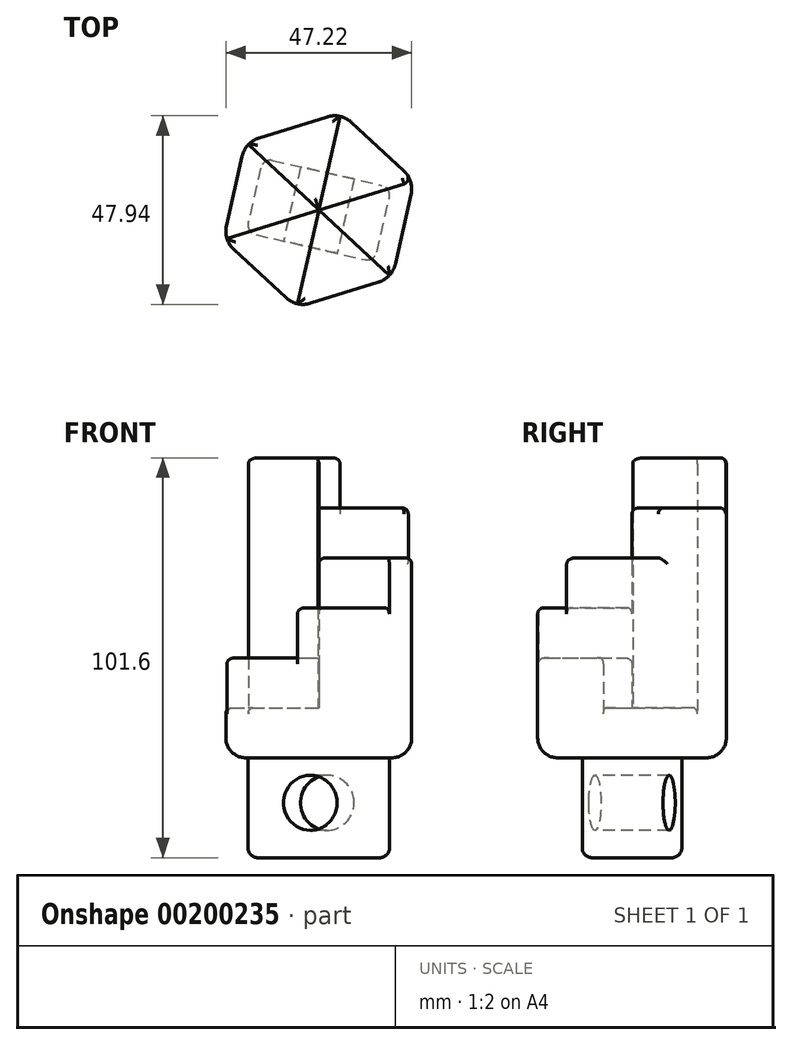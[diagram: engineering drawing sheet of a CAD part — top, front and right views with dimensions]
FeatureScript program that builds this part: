
annotation { "Feature Type Name" : "Feature", "Feature Type Description" : "" }
export const myFeature = defineFeature(function(context is Context, id is Id, definition is map)
    precondition{}
    {
        {
            var Q0;
            Q0=qCreatedBy(makeId("Top.planeOp"),FACE);
            var sketch = newSketch(context, id + "F0", { "sketchPlane" : qUnion([Q0])});
            skLineSegment(sketch, "E0.0", {"start": v(23.45, 3.92) * mm, "end": v(19.44, -13.7) * mm});
            skLineSegment(sketch, "E0.1", {"start": v(15.12, -18.35) * mm, "end": v(-2.14, -23.68) * mm});
            skLineSegment(sketch, "E0.2", {"start": v(-8.33, -22.27) * mm, "end": v(-21.58, -10) * mm});
            skLineSegment(sketch, "E0.3", {"start": v(-23.45, -3.92) * mm, "end": v(-19.44, 13.7) * mm});
            skLineSegment(sketch, "E0.4", {"start": v(-15.12, 18.35) * mm, "end": v(2.14, 23.68) * mm});
            skLineSegment(sketch, "E0.5", {"start": v(8.33, 22.27) * mm, "end": v(21.58, 10) * mm});
            skPoint(sketch, "E1", {"position": v(0, 0) * mm});
            skLineSegment(sketch, "E2", {"start": v(-24.27, -7.5) * mm, "end": v(24.27, 7.5) * mm});
            skLineSegment(sketch, "E3", {"start": v(-18.63, 17.27) * mm, "end": v(18.63, -17.27) * mm});
            skLineSegment(sketch, "E4", {"start": v(5.64, 24.77) * mm, "end": v(-5.64, -24.77) * mm});
            skPoint(sketch, "E5.visualSharp", {"position": v(-18.63, 17.27) * mm});
            skArc(sketch, "E5.filletArc", {"start": v(-15.12, 18.35) * mm, "mid": v(-17.9, 16.6) * mm, "end": v(-19.44, 13.7) * mm});
            skPoint(sketch, "E6.visualSharp", {"position": v(5.64, 24.77) * mm});
            skArc(sketch, "E6.filletArc", {"start": v(8.33, 22.27) * mm, "mid": v(5.42, 23.8) * mm, "end": v(2.14, 23.68) * mm});
            skPoint(sketch, "E7.visualSharp", {"position": v(24.27, 7.5) * mm});
            skArc(sketch, "E7.filletArc", {"start": v(23.45, 3.92) * mm, "mid": v(23.33, 7.2) * mm, "end": v(21.58, 10) * mm});
            skPoint(sketch, "E8.visualSharp", {"position": v(18.63, -17.27) * mm});
            skArc(sketch, "E8.filletArc", {"start": v(15.12, -18.35) * mm, "mid": v(17.9, -16.6) * mm, "end": v(19.44, -13.7) * mm});
            skPoint(sketch, "E9.visualSharp", {"position": v(-5.64, -24.77) * mm});
            skArc(sketch, "E9.filletArc", {"start": v(-8.33, -22.27) * mm, "mid": v(-5.42, -23.8) * mm, "end": v(-2.14, -23.68) * mm});
            skPoint(sketch, "E10.visualSharp", {"position": v(-24.27, -7.5) * mm});
            skArc(sketch, "E10.filletArc", {"start": v(-23.45, -3.92) * mm, "mid": v(-23.33, -7.2) * mm, "end": v(-21.58, -10) * mm});
            skSolve(sketch);
        }
        {
            var Q0;
            {var subQ1=sQuery(id+"F0.wireOp",EDGE,"E0.5");Q0=makeQuery(id+"F0.imprint","IMPRINT",FACE,{"disambiguationData":[TD([[makeQuery(id+"F0.imprint","IMPRINT",EDGE,{"derivedFrom":subQ1}),-1.0]])]});}
            var Q1;
            {var subQ7=sQuery(id+"F0.wireOp",EDGE,"E0.0");Q1=makeQuery(id+"F0.imprint","IMPRINT",FACE,{"disambiguationData":[TD([[makeQuery(id+"F0.imprint","IMPRINT",EDGE,{"derivedFrom":subQ7}),-1.0]])]});}
            var Q2;
            {var subQ7=sQuery(id+"F0.wireOp",EDGE,"E0.1");Q2=makeQuery(id+"F0.imprint","IMPRINT",FACE,{"disambiguationData":[TD([[makeQuery(id+"F0.imprint","IMPRINT",EDGE,{"derivedFrom":subQ7}),-1.0]])]});}
            var Q3;
            {var subQ5=sQuery(id+"F0.wireOp",EDGE,"E0.2");Q3=makeQuery(id+"F0.imprint","IMPRINT",FACE,{"disambiguationData":[TD([[makeQuery(id+"F0.imprint","IMPRINT",EDGE,{"derivedFrom":subQ5}),-1.0]])]});}
            var Q4;
            {var subQ1=sQuery(id+"F0.wireOp",EDGE,"E0.4");Q4=makeQuery(id+"F0.imprint","IMPRINT",FACE,{"disambiguationData":[TD([[makeQuery(id+"F0.imprint","IMPRINT",EDGE,{"derivedFrom":subQ1}),-1.0]])]});}
            var Q5;
            {var subQ1=sQuery(id+"F0.wireOp",EDGE,"E0.3");Q5=makeQuery(id+"F0.imprint","IMPRINT",FACE,{"disambiguationData":[TD([[makeQuery(id+"F0.imprint","IMPRINT",EDGE,{"derivedFrom":subQ1}),-1.0]])]});}
            extrude(context, id + "F1", {"entities" : qUnion([Q0, Q1, Q2, Q3, Q4, Q5]), "depth" : 12.7 * mm});
        }
        {
            var Q0;
            Q0=makeQuery(id+"F1.opExtrude","CAP_FACE",FACE,{"disambiguationData":[OSD([sQuery(id+"F0.wireOp",EDGE,"E0.0"),sQuery(id+"F0.wireOp",EDGE,"E0.1"),sQuery(id+"F0.wireOp",EDGE,"E0.2"),sQuery(id+"F0.wireOp",EDGE,"E0.3"),sQuery(id+"F0.wireOp",EDGE,"E0.4"),sQuery(id+"F0.wireOp",EDGE,"E0.5"),sQuery(id+"F0.wireOp",EDGE,"E5.filletArc"),sQuery(id+"F0.wireOp",EDGE,"E6.filletArc"),sQuery(id+"F0.wireOp",EDGE,"E7.filletArc"),sQuery(id+"F0.wireOp",EDGE,"E8.filletArc"),sQuery(id+"F0.wireOp",EDGE,"E9.filletArc"),sQuery(id+"F0.wireOp",EDGE,"E10.filletArc")])],"isStart":false});
            var sketch = newSketch(context, id + "F2", { "sketchPlane" : qUnion([Q0])});
            skLineSegment(sketch, "E11", {"start": v(-0.2, 0.19) * mm, "end": v(0, 0) * mm});
            skPoint(sketch, "E12", {"position": v(0, 0) * mm});
            skLineSegment(sketch, "E13", {"start": v(0, 0) * mm, "end": v(0.06, 0.27) * mm});
            skLineSegment(sketch, "E14", {"start": v(-0.2, 0.19) * mm, "end": v(0.06, 0.27) * mm});
            skPoint(sketch, "E15.orphan", {"position": v(-17.9, 16.6) * mm});
            skPoint(sketch, "E16.orphan", {"position": v(5.42, 23.8) * mm});
            skPoint(sketch, "E17.orphan", {"position": v(23.33, 7.2) * mm});
            skPoint(sketch, "E18.orphan", {"position": v(17.9, -16.6) * mm});
            skPoint(sketch, "E19.orphan", {"position": v(-5.42, -23.8) * mm});
            skPoint(sketch, "E20.orphan", {"position": v(-23.45, -6.74) * mm});
            skLineSegment(sketch, "E21", {"start": v(-17.9, 16.6) * mm, "end": v(17.9, -16.6) * mm});
            skSolve(sketch);
        }
        {
            var Q0;
            {var subQ5=sQuery(id+"F2.wireOp",EDGE,"E13");Q0=makeQuery(id+"F2.imprint","IMPRINT",FACE,{"disambiguationData":[TD([[makeQuery(id+"F2.imprint","IMPRINT",EDGE,{"derivedFrom":subQ5}),-1.0]])]});}
            extrude(context, id + "F3", {"entities" : qUnion([Q0]), "operationType" : NewBodyOperationType.ADD, "depth" : 38.1 * mm});
        }
        {
            var Q0;
            Q0=makeQuery(id+"F1.opExtrude","CAP_FACE",FACE,{"disambiguationData":[OSD([sQuery(id+"F0.wireOp",EDGE,"E0.0"),sQuery(id+"F0.wireOp",EDGE,"E0.1"),sQuery(id+"F0.wireOp",EDGE,"E0.2"),sQuery(id+"F0.wireOp",EDGE,"E0.3"),sQuery(id+"F0.wireOp",EDGE,"E0.4"),sQuery(id+"F0.wireOp",EDGE,"E0.5"),sQuery(id+"F0.wireOp",EDGE,"E5.filletArc"),sQuery(id+"F0.wireOp",EDGE,"E6.filletArc"),sQuery(id+"F0.wireOp",EDGE,"E7.filletArc"),sQuery(id+"F0.wireOp",EDGE,"E8.filletArc"),sQuery(id+"F0.wireOp",EDGE,"E9.filletArc"),sQuery(id+"F0.wireOp",EDGE,"E10.filletArc")])],"isStart":false});
            var sketch = newSketch(context, id + "F4", { "sketchPlane" : qUnion([Q0])});
            skLineSegment(sketch, "E22", {"start": v(-23.33, -7.2) * mm, "end": v(0, 0) * mm});
            skSolve(sketch);
        }
        {
            var Q0;
            {var subQ1=sQuery(id+"F4.wireOp",EDGE,"E22");Q0=makeQuery(id+"F4.imprint","IMPRINT",FACE,{"disambiguationData":[TD([[makeQuery(id+"F4.imprint","IMPRINT",EDGE,{"derivedFrom":subQ1}),-1.0]])]});}
            extrude(context, id + "F5", {"entities" : qUnion([Q0]), "operationType" : NewBodyOperationType.ADD, "depth" : 12.7 * mm});
        }
        {
            var Q0;
            Q0=makeQuery(id+"F5.opExtrude","CAP_FACE",FACE,{"disambiguationData":[OSD([sQuery(id+"F0.wireOp",EDGE,"E0.1"),sQuery(id+"F0.wireOp",EDGE,"E0.2"),sQuery(id+"F0.wireOp",EDGE,"E8.filletArc"),sQuery(id+"F0.wireOp",EDGE,"E9.filletArc"),sQuery(id+"F0.wireOp",EDGE,"E10.filletArc"),sQuery(id+"F2.wireOp",EDGE,"E21"),sQuery(id+"F4.wireOp",EDGE,"E22")])],"isStart":false});
            var sketch = newSketch(context, id + "F6", { "sketchPlane" : qUnion([Q0])});
            skLineSegment(sketch, "E23", {"start": v(-5.42, -23.8) * mm, "end": v(0, 0) * mm});
            skSolve(sketch);
        }
        {
            var Q0;
            {var subQ2=sQuery(id+"F6.wireOp",EDGE,"E23");Q0=makeQuery(id+"F6.imprint","IMPRINT",FACE,{"disambiguationData":[TD([[makeQuery(id+"F6.imprint","IMPRINT",EDGE,{"derivedFrom":subQ2}),-1.0]])]});}
            extrude(context, id + "F7", {"entities" : qUnion([Q0]), "operationType" : NewBodyOperationType.ADD, "depth" : 12.7 * mm});
        }
        {
            var Q0;
            Q0=makeQuery(id+"F3.opExtrude","CAP_FACE",FACE,{"disambiguationData":[OSD([sQuery(id+"F0.wireOp",EDGE,"E0.0"),sQuery(id+"F0.wireOp",EDGE,"E0.4"),sQuery(id+"F0.wireOp",EDGE,"E0.5"),sQuery(id+"F0.wireOp",EDGE,"E5.filletArc"),sQuery(id+"F0.wireOp",EDGE,"E6.filletArc"),sQuery(id+"F0.wireOp",EDGE,"E7.filletArc"),sQuery(id+"F0.wireOp",EDGE,"E8.filletArc"),sQuery(id+"F2.wireOp",EDGE,"E13"),sQuery(id+"F2.wireOp",EDGE,"E14"),sQuery(id+"F2.wireOp",EDGE,"E21")])],"isStart":false});
            var sketch = newSketch(context, id + "F8", { "sketchPlane" : qUnion([Q0])});
            skLineSegment(sketch, "E24", {"start": v(23.45, 7.2) * mm, "end": v(0, 0) * mm});
            skPoint(sketch, "E24.startSnap0", {"position": v(23.33, 7.2) * mm});
            skSolve(sketch);
        }
        {
            var Q0;
            {var subQ3=sQuery(id+"F2.wireOp",EDGE,"E13");var subQ4=makeQuery(id+"F3.opExtrude","CAP_EDGE",EDGE,{"disambiguationData":[OSD([subQ3])],"isStart":false});Q0=makeQuery(id+"F8.imprint","IMPRINT",FACE,{"disambiguationData":[TD([[makeQuery(id+"F8.imprint","IMPRINT",EDGE,{"derivedFrom":subQ4}),-1.0]])]});}
            extrude(context, id + "F9", {"entities" : qUnion([Q0]), "operationType" : NewBodyOperationType.ADD, "depth" : 12.7 * mm});
        }
        {
            var Q0;
            Q0=makeQuery(id+"F9.opExtrude","CAP_FACE",FACE,{"disambiguationData":[OSD([sQuery(id+"F0.wireOp",EDGE,"E0.4"),sQuery(id+"F0.wireOp",EDGE,"E0.5"),sQuery(id+"F0.wireOp",EDGE,"E5.filletArc"),sQuery(id+"F0.wireOp",EDGE,"E6.filletArc"),sQuery(id+"F0.wireOp",EDGE,"E7.filletArc"),sQuery(id+"F2.wireOp",EDGE,"E13"),sQuery(id+"F2.wireOp",EDGE,"E14"),sQuery(id+"F2.wireOp",EDGE,"E21"),sQuery(id+"F8.wireOp",EDGE,"E24")])],"isStart":false});
            var sketch = newSketch(context, id + "F10", { "sketchPlane" : qUnion([Q0])});
            skLineSegment(sketch, "E25", {"start": v(0, 0) * mm, "end": v(5.42, 23.8) * mm});
            skSolve(sketch);
        }
        {
            var Q0;
            {var subQ2=makeQuery(id+"F9.opExtrude","CAP_EDGE",EDGE,{"disambiguationData":[OSD([sQuery(id+"F2.wireOp",EDGE,"E14")])],"isStart":false});Q0=makeQuery(id+"F10.imprint","IMPRINT",FACE,{"disambiguationData":[TD([[makeQuery(id+"F10.imprint","IMPRINT",EDGE,{"derivedFrom":subQ2}),1.0]])]});}
            extrude(context, id + "F11", {"entities" : qUnion([Q0]), "operationType" : NewBodyOperationType.ADD, "depth" : 12.7 * mm});
        }
        {
            var Q0;
            Q0=makeQuery(id+"F1.opExtrude","CAP_FACE",FACE,{"disambiguationData":[OSD([sQuery(id+"F0.wireOp",EDGE,"E0.0"),sQuery(id+"F0.wireOp",EDGE,"E0.1"),sQuery(id+"F0.wireOp",EDGE,"E0.2"),sQuery(id+"F0.wireOp",EDGE,"E0.3"),sQuery(id+"F0.wireOp",EDGE,"E0.4"),sQuery(id+"F0.wireOp",EDGE,"E0.5"),sQuery(id+"F0.wireOp",EDGE,"E5.filletArc"),sQuery(id+"F0.wireOp",EDGE,"E6.filletArc"),sQuery(id+"F0.wireOp",EDGE,"E7.filletArc"),sQuery(id+"F0.wireOp",EDGE,"E8.filletArc"),sQuery(id+"F0.wireOp",EDGE,"E9.filletArc"),sQuery(id+"F0.wireOp",EDGE,"E10.filletArc")])],"isStart":true});
            fillet(context, id + "F12", {"entities" : qUnion([Q0]), "radius" : 5.08 * mm, "tangentPropagation" : true, "allowEdgeOverflow" : false});
        }
        {
            var Q0;
            Q0=makeQuery(id+"F1.opExtrude","CAP_FACE",FACE,{"disambiguationData":[OSD([sQuery(id+"F0.wireOp",EDGE,"E0.0"),sQuery(id+"F0.wireOp",EDGE,"E0.1"),sQuery(id+"F0.wireOp",EDGE,"E0.2"),sQuery(id+"F0.wireOp",EDGE,"E0.3"),sQuery(id+"F0.wireOp",EDGE,"E0.4"),sQuery(id+"F0.wireOp",EDGE,"E0.5"),sQuery(id+"F0.wireOp",EDGE,"E5.filletArc"),sQuery(id+"F0.wireOp",EDGE,"E6.filletArc"),sQuery(id+"F0.wireOp",EDGE,"E7.filletArc"),sQuery(id+"F0.wireOp",EDGE,"E8.filletArc"),sQuery(id+"F0.wireOp",EDGE,"E9.filletArc"),sQuery(id+"F0.wireOp",EDGE,"E10.filletArc")])],"isStart":true});
            var sketch = newSketch(context, id + "F13", { "sketchPlane" : qUnion([Q0])});
            skPoint(sketch, "E26", {"position": v(0, 0) * mm});
            skPoint(sketch, "E27.orphan", {"position": v(-16.5, -3.76) * mm});
            skPoint(sketch, "E28.end.orphan", {"position": v(16.5, 3.76) * mm});
            skPoint(sketch, "E29", {"position": v(-14.18, -13.15) * mm});
            skPoint(sketch, "E30", {"position": v(14.18, 13.15) * mm});
            skPoint(sketch, "E31", {"position": v(18.48, -6.26) * mm});
            skPoint(sketch, "E31.positionSnap0", {"position": v(18.48, -5.7) * mm});
            skPoint(sketch, "E32", {"position": v(4.3, -18.85) * mm});
            skPoint(sketch, "E33", {"position": v(-3.73, 18.85) * mm});
            skPoint(sketch, "E33.positionSnap0", {"position": v(-4.3, 18.85) * mm});
            skPoint(sketch, "E34", {"position": v(-18.13, 5.7) * mm});
            skPoint(sketch, "E34.positionSnap0", {"position": v(-18.48, 5.7) * mm});
            skPoint(sketch, "E35.start.orphan", {"position": v(-8.25, -1.88) * mm});
            skPoint(sketch, "E36.start.orphan", {"position": v(8.25, 1.88) * mm});
            skLineSegment(sketch, "E37", {"start": v(-14.18, -13.15) * mm, "end": v(18.48, -5.7) * mm});
            skLineSegment(sketch, "E38", {"start": v(-18.48, 5.7) * mm, "end": v(14.18, 13.15) * mm});
            skLineSegment(sketch, "E39", {"start": v(-14.18, -13.15) * mm, "end": v(-18.48, 5.7) * mm});
            skLineSegment(sketch, "E40", {"start": v(14.18, 13.15) * mm, "end": v(18.48, -5.7) * mm});
            skSolve(sketch);
        }
        {
            var Q0;
            Q0=makeQuery(id+"F11.opExtrude","CAP_FACE",FACE,{"disambiguationData":[OSD([sQuery(id+"F0.wireOp",EDGE,"E0.4"),sQuery(id+"F0.wireOp",EDGE,"E5.filletArc"),sQuery(id+"F0.wireOp",EDGE,"E6.filletArc"),sQuery(id+"F2.wireOp",EDGE,"E14"),sQuery(id+"F2.wireOp",EDGE,"E21"),sQuery(id+"F10.wireOp",EDGE,"E25")])],"isStart":false});
            fillet(context, id + "F14", {"entities" : qUnion([Q0]), "radius" : 1.52 * mm, "tangentPropagation" : true, "allowEdgeOverflow" : false});
        }
        {
            var Q0;
            Q0=makeQuery(id+"F9.opExtrude","CAP_EDGE",EDGE,{"disambiguationData":[OSD([sQuery(id+"F8.wireOp",EDGE,"E24")])],"isStart":false});
            fillet(context, id + "F15", {"entities" : qUnion([Q0]), "radius" : 1.52 * mm, "tangentPropagation" : true, "allowEdgeOverflow" : false});
        }
        {
            var Q0;
            Q0=makeQuery(id+"F9.opExtrude","CAP_EDGE",EDGE,{"disambiguationData":[OSD([sQuery(id+"F0.wireOp",EDGE,"E0.5")])],"isStart":false});
            fillet(context, id + "F16", {"entities" : qUnion([Q0]), "radius" : 1.52 * mm, "tangentPropagation" : true, "allowEdgeOverflow" : false});
        }
        {
            var Q0;
            Q0=makeQuery(id+"F3.opExtrude","CAP_EDGE",EDGE,{"disambiguationData":[OSD([sQuery(id+"F0.wireOp",EDGE,"E0.0")])],"isStart":false});
            var Q1;
            {var subQ0=sQuery(id+"F2.wireOp",EDGE,"E21");Q1=makeQuery(id+"F3.opExtrude","CAP_EDGE",EDGE,{"disambiguationData":[OSD([subQ0]),TDD([makeQuery(id+"F2.imprint","IMPRINT",EDGE,{"disambiguationData":[TD([[makeQuery(id+"F2.imprint","INTERSECT",VERTEX,{"derivedFrom":[sQuery(id+"F2.wireOp",EDGE,"E13"),subQ0]}),-1.0]])],"derivedFrom":subQ0})])],"isStart":false});}
            fillet(context, id + "F17", {"entities" : qUnion([Q0, Q1]), "radius" : 1.52 * mm, "tangentPropagation" : true, "allowEdgeOverflow" : false});
        }
        {
            var Q0;
            Q0=makeQuery(id+"F7.opExtrude","CAP_EDGE",EDGE,{"disambiguationData":[OSD([sQuery(id+"F0.wireOp",EDGE,"E0.1")])],"isStart":false});
            var Q1;
            Q1=makeQuery(id+"F7.opExtrude","CAP_EDGE",EDGE,{"disambiguationData":[OSD([sQuery(id+"F6.wireOp",EDGE,"E23")])],"isStart":false});
            var Q2;
            Q2=makeQuery(id+"F7.opExtrude","CAP_EDGE",EDGE,{"disambiguationData":[OSD([sQuery(id+"F0.wireOp",EDGE,"E9.filletArc")])],"isStart":false});
            fillet(context, id + "F18", {"entities" : qUnion([Q0, Q1, Q2]), "radius" : 1.52 * mm, "tangentPropagation" : true, "allowEdgeOverflow" : false});
        }
        {
            var Q0;
            Q0=makeQuery(id+"F5.opExtrude","CAP_EDGE",EDGE,{"disambiguationData":[OSD([sQuery(id+"F0.wireOp",EDGE,"E0.2")])],"isStart":false});
            var Q1;
            Q1=makeQuery(id+"F5.opExtrude","CAP_EDGE",EDGE,{"disambiguationData":[OSD([sQuery(id+"F0.wireOp",EDGE,"E9.filletArc")])],"isStart":false});
            var Q2;
            Q2=makeQuery(id+"F5.opExtrude","CAP_EDGE",EDGE,{"disambiguationData":[OSD([sQuery(id+"F0.wireOp",EDGE,"E10.filletArc")])],"isStart":false});
            var Q3;
            Q3=makeQuery(id+"F5.opExtrude","CAP_EDGE",EDGE,{"disambiguationData":[OSD([sQuery(id+"F4.wireOp",EDGE,"E22")])],"isStart":false});
            fillet(context, id + "F19", {"entities" : qUnion([Q0, Q1, Q2, Q3]), "radius" : 1.52 * mm, "tangentPropagation" : true, "allowEdgeOverflow" : false});
        }
        {
            var Q0;
            Q0=makeQuery(id+"F1.opExtrude","CAP_EDGE",EDGE,{"disambiguationData":[OSD([sQuery(id+"F0.wireOp",EDGE,"E10.filletArc")])],"isStart":false});
            var Q1;
            Q1=makeQuery(id+"F1.opExtrude","CAP_EDGE",EDGE,{"disambiguationData":[OSD([sQuery(id+"F0.wireOp",EDGE,"E0.3")])],"isStart":false});
            var Q2;
            Q2=makeQuery(id+"F1.opExtrude","CAP_EDGE",EDGE,{"disambiguationData":[OSD([sQuery(id+"F0.wireOp",EDGE,"E5.filletArc")])],"isStart":false});
            fillet(context, id + "F20", {"entities" : qUnion([Q0, Q1, Q2]), "radius" : 1.52 * mm, "tangentPropagation" : true, "allowEdgeOverflow" : false});
        }
        {
            var Q0;
            Q0=makeQuery(id+"F13.imprint","IMPRINT",FACE,{"disambiguationData":[TD([[makeQuery(id+"F13.imprint","IMPRINT",EDGE,{"derivedFrom":sQuery(id+"F13.wireOp",EDGE,"E37")}),1.0]])]});
            extrude(context, id + "F21", {"entities" : qUnion([Q0]), "operationType" : NewBodyOperationType.ADD, "depth" : 25.4 * mm});
        }
        {
            var Q0;
            Q0=makeQuery(id+"F21.opExtrude","SWEPT_EDGE",EDGE,{"disambiguationData":[OSD([sQuery(id+"F0.wireOp",EDGE,"E0.0"),sQuery(id+"F0.wireOp",EDGE,"E0.1"),sQuery(id+"F0.wireOp",EDGE,"E0.2"),sQuery(id+"F0.wireOp",EDGE,"E0.3"),sQuery(id+"F0.wireOp",EDGE,"E0.4"),sQuery(id+"F0.wireOp",EDGE,"E0.5"),sQuery(id+"F0.wireOp",EDGE,"E5.filletArc"),sQuery(id+"F0.wireOp",EDGE,"E6.filletArc"),sQuery(id+"F0.wireOp",EDGE,"E7.filletArc"),sQuery(id+"F0.wireOp",EDGE,"E8.filletArc"),sQuery(id+"F0.wireOp",EDGE,"E9.filletArc"),sQuery(id+"F0.wireOp",EDGE,"E10.filletArc"),sQuery(id+"F13.wireOp",EDGE,"E37"),sQuery(id+"F13.wireOp",EDGE,"E39")])]});
            var Q1;
            Q1=makeQuery(id+"F21.opExtrude","SWEPT_EDGE",EDGE,{"disambiguationData":[OSD([sQuery(id+"F0.wireOp",EDGE,"E0.0"),sQuery(id+"F0.wireOp",EDGE,"E0.1"),sQuery(id+"F0.wireOp",EDGE,"E0.2"),sQuery(id+"F0.wireOp",EDGE,"E0.3"),sQuery(id+"F0.wireOp",EDGE,"E0.4"),sQuery(id+"F0.wireOp",EDGE,"E0.5"),sQuery(id+"F0.wireOp",EDGE,"E5.filletArc"),sQuery(id+"F0.wireOp",EDGE,"E6.filletArc"),sQuery(id+"F0.wireOp",EDGE,"E7.filletArc"),sQuery(id+"F0.wireOp",EDGE,"E8.filletArc"),sQuery(id+"F0.wireOp",EDGE,"E9.filletArc"),sQuery(id+"F0.wireOp",EDGE,"E10.filletArc"),sQuery(id+"F13.wireOp",EDGE,"E38"),sQuery(id+"F13.wireOp",EDGE,"E39")])]});
            var Q2;
            Q2=makeQuery(id+"F21.opExtrude","SWEPT_EDGE",EDGE,{"disambiguationData":[OSD([sQuery(id+"F0.wireOp",EDGE,"E0.0"),sQuery(id+"F0.wireOp",EDGE,"E0.1"),sQuery(id+"F0.wireOp",EDGE,"E0.2"),sQuery(id+"F0.wireOp",EDGE,"E0.3"),sQuery(id+"F0.wireOp",EDGE,"E0.4"),sQuery(id+"F0.wireOp",EDGE,"E0.5"),sQuery(id+"F0.wireOp",EDGE,"E5.filletArc"),sQuery(id+"F0.wireOp",EDGE,"E6.filletArc"),sQuery(id+"F0.wireOp",EDGE,"E7.filletArc"),sQuery(id+"F0.wireOp",EDGE,"E8.filletArc"),sQuery(id+"F0.wireOp",EDGE,"E9.filletArc"),sQuery(id+"F0.wireOp",EDGE,"E10.filletArc"),sQuery(id+"F13.wireOp",EDGE,"E37"),sQuery(id+"F13.wireOp",EDGE,"E40")])]});
            var Q3;
            Q3=makeQuery(id+"F21.opExtrude","SWEPT_EDGE",EDGE,{"disambiguationData":[OSD([sQuery(id+"F0.wireOp",EDGE,"E0.0"),sQuery(id+"F0.wireOp",EDGE,"E0.1"),sQuery(id+"F0.wireOp",EDGE,"E0.2"),sQuery(id+"F0.wireOp",EDGE,"E0.3"),sQuery(id+"F0.wireOp",EDGE,"E0.4"),sQuery(id+"F0.wireOp",EDGE,"E0.5"),sQuery(id+"F0.wireOp",EDGE,"E5.filletArc"),sQuery(id+"F0.wireOp",EDGE,"E6.filletArc"),sQuery(id+"F0.wireOp",EDGE,"E7.filletArc"),sQuery(id+"F0.wireOp",EDGE,"E8.filletArc"),sQuery(id+"F0.wireOp",EDGE,"E9.filletArc"),sQuery(id+"F0.wireOp",EDGE,"E10.filletArc"),sQuery(id+"F13.wireOp",EDGE,"E38"),sQuery(id+"F13.wireOp",EDGE,"E40")])]});
            fillet(context, id + "F22", {"entities" : qUnion([Q0, Q1, Q2, Q3]), "radius" : 2.54 * mm, "tangentPropagation" : true, "allowEdgeOverflow" : false});
        }
        {
            var Q0;
            Q0=makeQuery(id+"F21.opExtrude","CAP_FACE",FACE,{"disambiguationData":[OSD([sQuery(id+"F13.wireOp",EDGE,"E37"),sQuery(id+"F13.wireOp",EDGE,"E38"),sQuery(id+"F13.wireOp",EDGE,"E39"),sQuery(id+"F13.wireOp",EDGE,"E40")])],"isStart":false});
            fillet(context, id + "F23", {"entities" : qUnion([Q0]), "radius" : 2.54 * mm, "tangentPropagation" : true, "allowEdgeOverflow" : false});
        }
        {
            var Q0;
            Q0=makeQuery(id+"F21.opExtrude","SWEPT_FACE",FACE,{"disambiguationData":[OSD([sQuery(id+"F13.wireOp",EDGE,"E38")])]});
            var sketch = newSketch(context, id + "F24", { "sketchPlane" : qUnion([Q0])});
            skPoint(sketch, "E41", {"position": v(0, -22.86) * mm});
            skPoint(sketch, "E42", {"position": v(0, -11.43) * mm});
            skPoint(sketch, "E43.orphan", {"position": v(14.2, -11.43) * mm});
            skPoint(sketch, "E44.end.orphan", {"position": v(-14.2, -11.43) * mm});
            skSolve(sketch);
        }
        {
            var Q0;
            Q0=sQuery(id+"F24.wireOp",VERTEX,"E42");
            var Q1;
            Q1=makeQuery(id+"F1.opExtrude","SWEPT_BODY",BODY,{"disambiguationData":[OSD([sQuery(id+"F0.wireOp",EDGE,"E0.0"),sQuery(id+"F0.wireOp",EDGE,"E0.1"),sQuery(id+"F0.wireOp",EDGE,"E0.2"),sQuery(id+"F0.wireOp",EDGE,"E0.3"),sQuery(id+"F0.wireOp",EDGE,"E0.4"),sQuery(id+"F0.wireOp",EDGE,"E0.5"),sQuery(id+"F0.wireOp",EDGE,"E5.filletArc"),sQuery(id+"F0.wireOp",EDGE,"E6.filletArc"),sQuery(id+"F0.wireOp",EDGE,"E7.filletArc"),sQuery(id+"F0.wireOp",EDGE,"E8.filletArc"),sQuery(id+"F0.wireOp",EDGE,"E9.filletArc"),sQuery(id+"F0.wireOp",EDGE,"E10.filletArc")])]});
            hole(context, id + "F25", {"style" : HoleStyle.SIMPLE, "endStyle" : HoleEndStyle.THROUGH, "holeDiameter" : 13.97 * mm, "locations" : qUnion([Q0]), "scope" : qUnion([Q1]), "isTappedThrough" : true});
        }
    });
